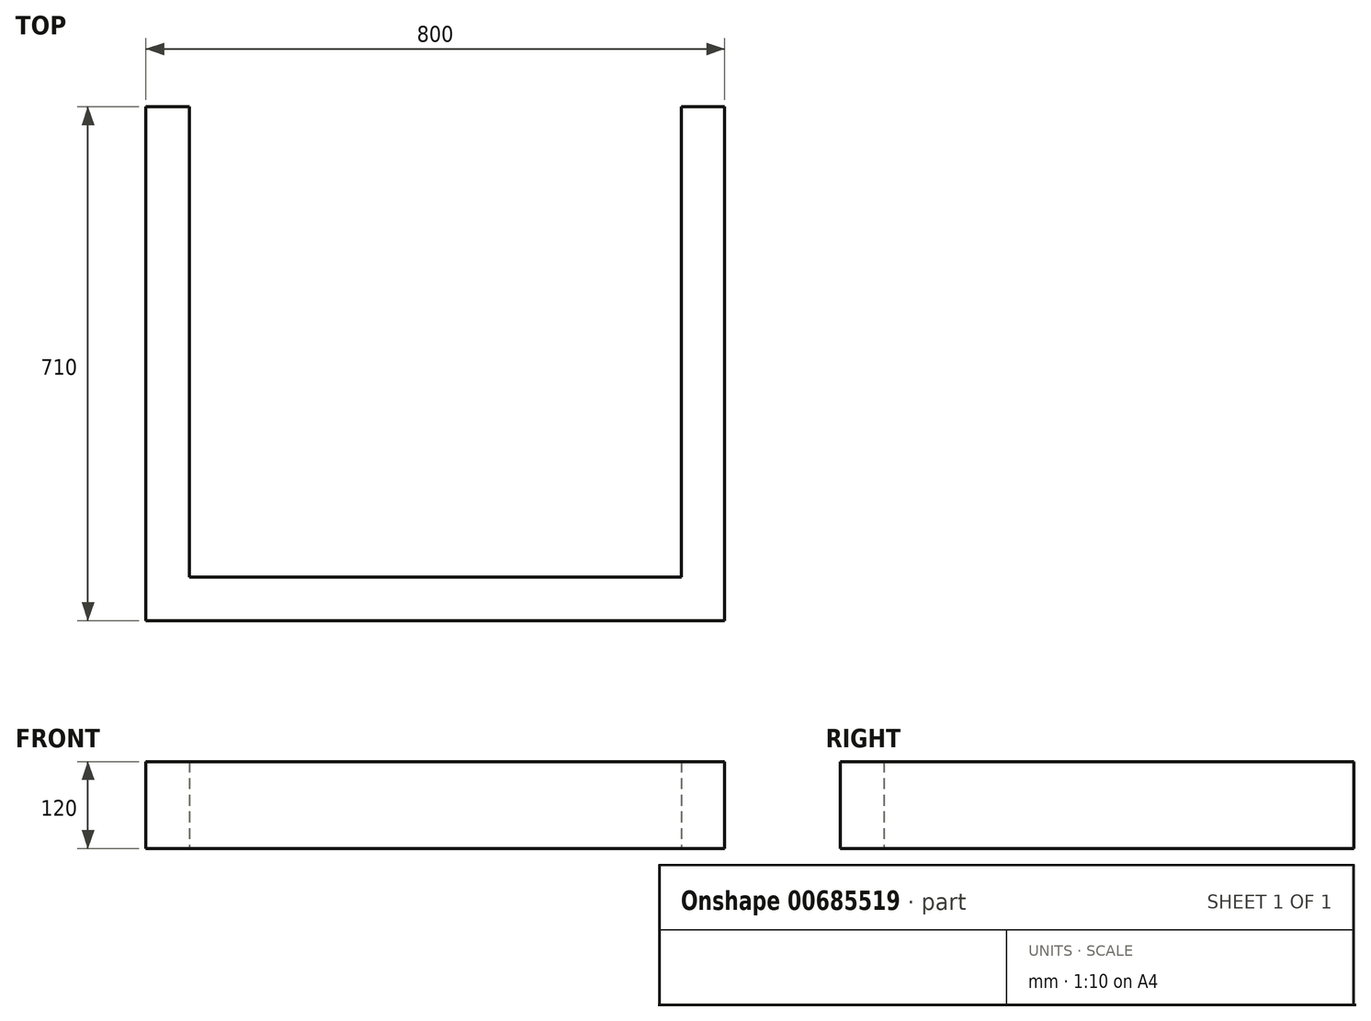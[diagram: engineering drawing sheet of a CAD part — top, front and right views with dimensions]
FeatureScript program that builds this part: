
annotation { "Feature Type Name" : "Feature", "Feature Type Description" : "" }
export const myFeature = defineFeature(function(context is Context, id is Id, definition is map)
    precondition{}
    {
        {
            var Q0;
            Q0=qCreatedBy(makeId("Top.planeOp"),FACE);
            var sketch = newSketch(context, id + "F0", { "sketchPlane" : qUnion([Q0])});
            skLineSegment(sketch, "E0", {"start": v(-400, 351.64) * mm, "end": v(-400, -358.36) * mm});
            skLineSegment(sketch, "E1", {"start": v(-400, -358.36) * mm, "end": v(0, -358.36) * mm});
            skLineSegment(sketch, "E2", {"start": v(0, -358.36) * mm, "end": v(0, -298.36) * mm});
            skLineSegment(sketch, "E3", {"start": v(0, -298.36) * mm, "end": v(-340, -298.36) * mm});
            skLineSegment(sketch, "E4", {"start": v(-340, -298.36) * mm, "end": v(-340, 351.64) * mm});
            skLineSegment(sketch, "E5", {"start": v(-340, 351.64) * mm, "end": v(-400, 351.64) * mm});
            skLineSegment(sketch, "E6.MirrorCS", {"start": v(400, 351.64) * mm, "end": v(400, -358.36) * mm});
            skLineSegment(sketch, "E7.MirrorCS", {"start": v(400, -358.36) * mm, "end": v(0, -358.36) * mm});
            skLineSegment(sketch, "E8.MirrorCS", {"start": v(340, -298.36) * mm, "end": v(340, 351.64) * mm});
            skLineSegment(sketch, "E9.MirrorCS", {"start": v(340, 351.64) * mm, "end": v(400, 351.64) * mm});
            skLineSegment(sketch, "E10.MirrorCS", {"start": v(0, -298.36) * mm, "end": v(340, -298.36) * mm});
            skSolve(sketch);
        }
        {
            var Q0;
            Q0=makeQuery(id+"F0.imprint","IMPRINT",FACE,{"disambiguationData":[TD([[makeQuery(id+"F0.imprint","IMPRINT",EDGE,{"derivedFrom":sQuery(id+"F0.wireOp",EDGE,"E0")}),1.0]])]});
            var Q1;
            Q1=makeQuery(id+"F0.imprint","IMPRINT",FACE,{"disambiguationData":[TD([[makeQuery(id+"F0.imprint","IMPRINT",EDGE,{"derivedFrom":sQuery(id+"F0.wireOp",EDGE,"E6.MirrorCS")}),-1.0]])]});
            extrude(context, id + "F1", {"entities" : qUnion([Q0, Q1]), "depth" : 120 * mm, "offsetDistance" : 25 * mm});
        }
    });
